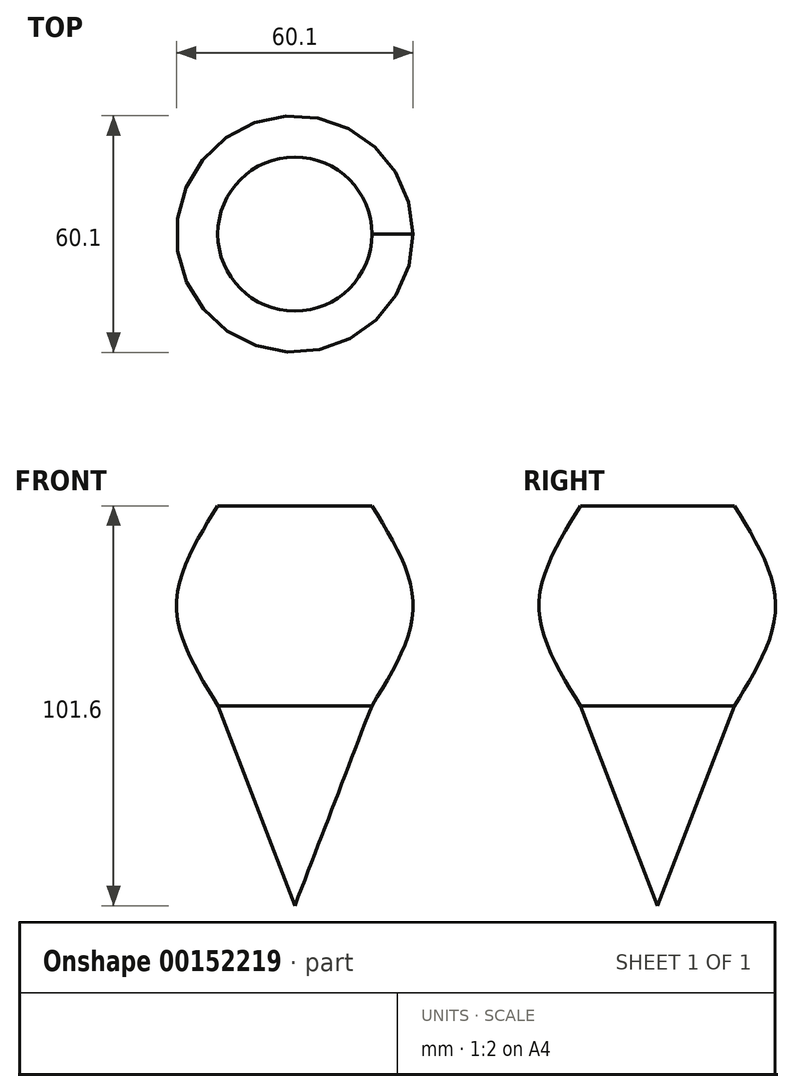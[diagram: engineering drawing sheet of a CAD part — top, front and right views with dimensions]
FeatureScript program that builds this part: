
annotation { "Feature Type Name" : "Feature", "Feature Type Description" : "" }
export const myFeature = defineFeature(function(context is Context, id is Id, definition is map)
    precondition{}
    {
        {
            var Q0;
            Q0=qCreatedBy(makeId("Top.planeOp"),FACE);
            var sketch = newSketch(context, id + "F0", { "sketchPlane" : qUnion([Q0])});
            skPoint(sketch, "E0", {"position": v(0, 0) * mm});
            skSolve(sketch);
        }
        {
            var Q0;
            Q0=qCreatedBy(makeId("Top.planeOp"),FACE);
            cPlane(context, id + "F1", {"entities" : qUnion([Q0]), "cplaneType" : CPlaneType.OFFSET, "offset" : 50.8 * mm, "width" : 152.4 * mm, "height" : 152.4 * mm});
        }
        {
            var Q0;
            Q0=qCreatedBy(id+"F1.planeOp",FACE);
            var sketch = newSketch(context, id + "F2", { "sketchPlane" : qUnion([Q0])});
            skCircle(sketch, "E1", {"center": v(0, 0) * mm, "radius": 19.54 * mm});
            skSolve(sketch);
        }
        {
            var Q0;
            Q0=makeQuery(id+"F2.imprint","IMPRINT",FACE,{"disambiguationData":[TD([[makeQuery(id+"F2.imprint","IMPRINT",EDGE,{"derivedFrom":sQuery(id+"F2.wireOp",EDGE,"E1")}),1.0]])]});
            var Q1;
            Q1=sQuery(id+"F0.wireOp",VERTEX,"E0");
            loft(context, id + "F3", {"sheetProfilesArray" : [{ "sheetProfileEntities" : qUnion([Q0]) }, { "sheetProfileEntities" : qUnion([Q1]) }]});
        }
        {
            var Q0;
            Q0=qCreatedBy(id+"F1.planeOp",FACE);
            cPlane(context, id + "F4", {"entities" : qUnion([Q0]), "cplaneType" : CPlaneType.OFFSET, "offset" : 25.4 * mm, "width" : 152.4 * mm, "height" : 152.4 * mm});
        }
        {
            var Q0;
            Q0=qCreatedBy(id+"F4.planeOp",FACE);
            var sketch = newSketch(context, id + "F5", { "sketchPlane" : qUnion([Q0])});
            skCircle(sketch, "E2", {"center": v(0, 0) * mm, "radius": 30.05 * mm});
            skSolve(sketch);
        }
        {
            var Q0;
            Q0=qCreatedBy(id+"F4.planeOp",FACE);
            cPlane(context, id + "F6", {"entities" : qUnion([Q0]), "cplaneType" : CPlaneType.OFFSET, "offset" : 25.4 * mm, "width" : 152.4 * mm, "height" : 152.4 * mm});
        }
        {
            var Q0;
            Q0=qCreatedBy(id+"F6.planeOp",FACE);
            var sketch = newSketch(context, id + "F7", { "sketchPlane" : qUnion([Q0])});
            skCircle(sketch, "E3", {"center": v(0, 0) * mm, "radius": 19.58 * mm});
            skSolve(sketch);
        }
        {
            var Q0;
            Q0=makeQuery(id+"F3.opLoft","CAP_FACE",FACE,{"disambiguationData":[OSD([makeQuery(id+"F2.imprint","IMPRINT",FACE,{"disambiguationData":[TD([[makeQuery(id+"F2.imprint","IMPRINT",EDGE,{"derivedFrom":sQuery(id+"F2.wireOp",EDGE,"E1")}),1.0]])]})])],"isStart":true});
            var Q1;
            Q1=makeQuery(id+"F5.imprint","IMPRINT",FACE,{"disambiguationData":[TD([[makeQuery(id+"F5.imprint","IMPRINT",EDGE,{"derivedFrom":sQuery(id+"F5.wireOp",EDGE,"E2")}),1.0]])]});
            var Q2;
            Q2=makeQuery(id+"F7.imprint","IMPRINT",FACE,{"disambiguationData":[TD([[makeQuery(id+"F7.imprint","IMPRINT",EDGE,{"derivedFrom":sQuery(id+"F7.wireOp",EDGE,"E3")}),1.0]])]});
            loft(context, id + "F8", {"sheetProfilesArray" : [{ "sheetProfileEntities" : qUnion([Q0]) }, { "sheetProfileEntities" : qUnion([Q1]) }, { "sheetProfileEntities" : qUnion([Q2]) }]});
        }
    });
